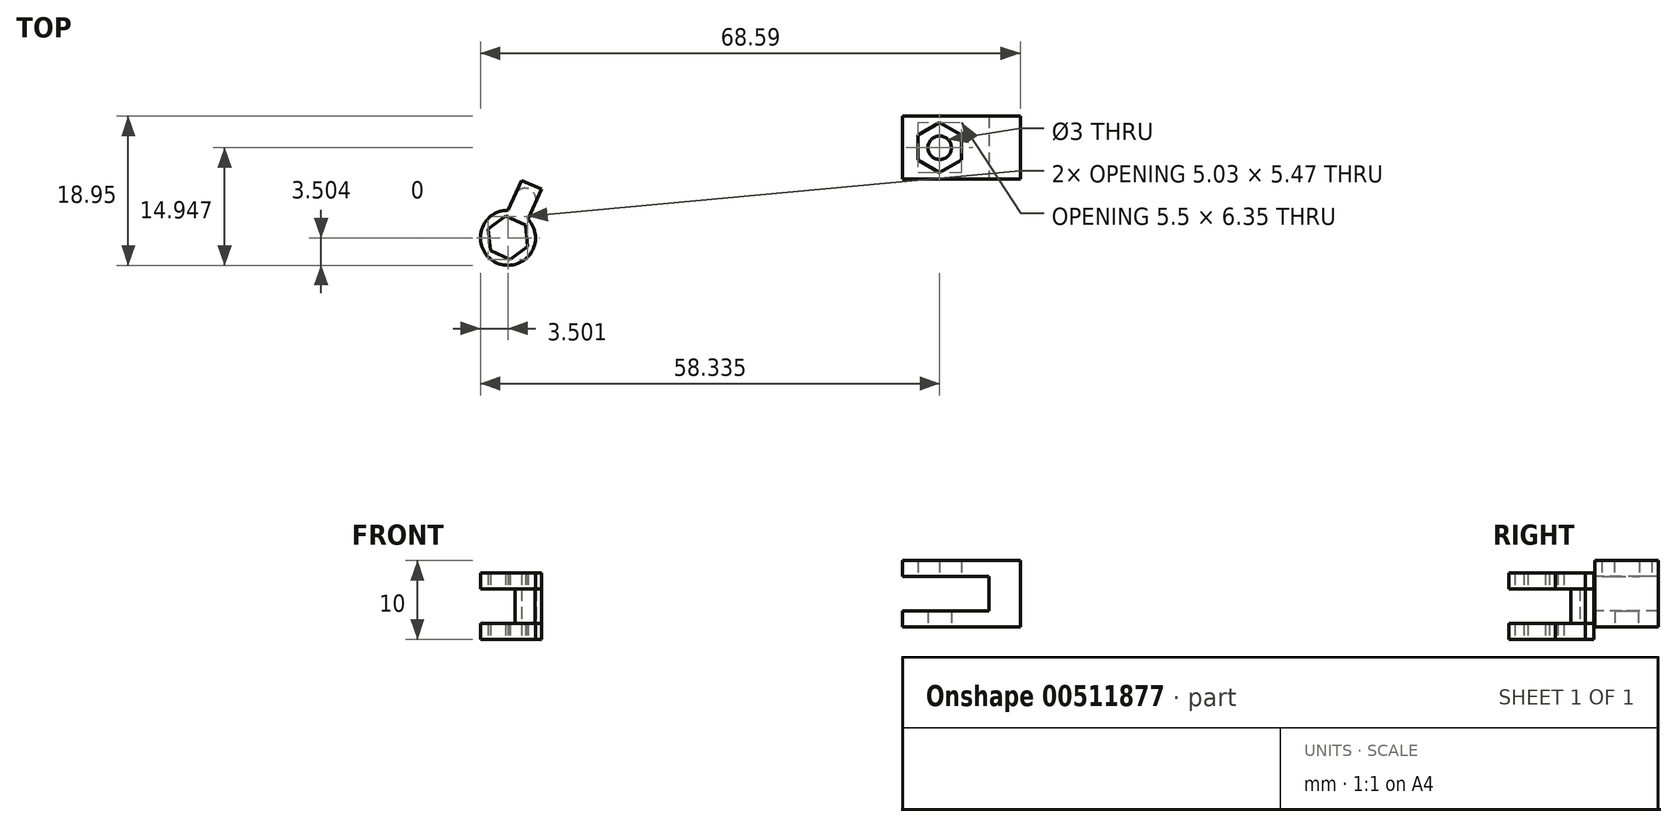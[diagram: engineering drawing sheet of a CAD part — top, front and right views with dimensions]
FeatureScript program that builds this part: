
annotation { "Feature Type Name" : "Feature", "Feature Type Description" : "" }
export const myFeature = defineFeature(function(context is Context, id is Id, definition is map)
    precondition{}
    {
        {
            var Q0;
            Q0=qCreatedBy(makeId("Top.planeOp"),FACE);
            var sketch = newSketch(context, id + "F0", { "sketchPlane" : qUnion([Q0])});
            skLineSegment(sketch, "E0.0", {"start": v(-17.86, 5.3) * mm, "end": v(-17.56, 2.57) * mm});
            skLineSegment(sketch, "E0.1", {"start": v(-17.56, 2.57) * mm, "end": v(-19.79, 0.95) * mm});
            skLineSegment(sketch, "E0.2", {"start": v(-19.79, 0.95) * mm, "end": v(-22.3, 2.06) * mm});
            skLineSegment(sketch, "E0.3", {"start": v(-22.3, 2.06) * mm, "end": v(-22.6, 4.8) * mm});
            skLineSegment(sketch, "E0.4", {"start": v(-22.6, 4.8) * mm, "end": v(-20.37, 6.42) * mm});
            skLineSegment(sketch, "E0.5", {"start": v(-20.37, 6.42) * mm, "end": v(-17.86, 5.3) * mm});
            skCircle(sketch, "E1", {"center": v(-20.08, 3.68) * mm, "radius": 3.5 * mm});
            skLineSegment(sketch, "E2", {"start": v(-20.37, 6.42) * mm, "end": v(-18.34, 10.99) * mm});
            skLineSegment(sketch, "E3", {"start": v(-17.86, 5.3) * mm, "end": v(-15.83, 9.88) * mm});
            skLineSegment(sketch, "E4", {"start": v(-15.83, 9.88) * mm, "end": v(-18.34, 10.99) * mm});
            skLineSegment(sketch, "E5", {"start": v(-20.37, 6.42) * mm, "end": v(-19.15, 9.16) * mm});
            skLineSegment(sketch, "E6", {"start": v(-16.64, 8.05) * mm, "end": v(-17.86, 5.3) * mm});
            skArc(sketch, "E7", {"start": v(-16.64, 8.05) * mm, "mid": v(-17.34, 9.86) * mm, "end": v(-19.15, 9.16) * mm});
            skSolve(sketch);
        }
        {
            var Q0;
            Q0 = qSketchRegion(id + "F0", true);
            var Q1;
            Q1 = qSketchRegion(id + "F2", true);
            extrude(context, id + "F1", {"entities" : qUnion([Q0, Q1]), "depth" : 8.4 * mm});
        }
        {
            var Q0;
            Q0=makeQuery(id+"F1.opExtrude","SWEPT_FACE",FACE,{"disambiguationData":[OSD([sQuery(id+"F0.wireOp",EDGE,"E3"),sQuery(id+"F0.wireOp",EDGE,"E6")])]});
            var sketch = newSketch(context, id + "F2", { "sketchPlane" : qUnion([Q0])});
            skLineSegment(sketch, "E8", {"start": v(2.61, 8.4) * mm, "end": v(2.61, 6.4) * mm});
            skLineSegment(sketch, "E9", {"start": v(2.61, 0) * mm, "end": v(2.61, 2) * mm});
            skLineSegment(sketch, "E10", {"start": v(2.61, 2) * mm, "end": v(-1.55, 2) * mm});
            skLineSegment(sketch, "E11", {"start": v(2.61, 6.4) * mm, "end": v(-1.55, 6.4) * mm});
            skLineSegment(sketch, "E12.bottom", {"start": v(2.61, 6.4) * mm, "end": v(-9.24, 6.4) * mm});
            skLineSegment(sketch, "E12.top", {"start": v(2.61, 2) * mm, "end": v(-9.24, 2) * mm});
            skLineSegment(sketch, "E12.left", {"start": v(2.61, 6.4) * mm, "end": v(2.61, 2) * mm});
            skLineSegment(sketch, "E12.right", {"start": v(-9.24, 6.4) * mm, "end": v(-9.24, 2) * mm});
            skSolve(sketch);
        }
        {
            var Q0;
            Q0 = qSketchRegion(id + "F2", true);
            extrude(context, id + "F3", {"entities" : qUnion([Q0]), "operationType" : NewBodyOperationType.REMOVE, "oppositeDirection" : true, "depth" : 25 * mm});
        }
        {
            var Q0;
            {var subQ0=sQuery(id+"F2.wireOp",EDGE,"E12.top");var subQ1=sQuery(id+"F2.wireOp",EDGE,"E12.bottom");Q0=makeQuery(id+"F3.boolean.opBoolean","COPY",FACE,{"disambiguationData":[TD([makeQuery(id+"F1.opExtrude","SWEPT_FACE",FACE,{"disambiguationData":[OSD([sQuery(id+"F0.wireOp",EDGE,"E0.1")])]})])],"derivedFrom":makeQuery(id+"F3.opExtrude","CAP_FACE",FACE,{"disambiguationData":[OSD([subQ1,subQ0,sQuery(id+"F2.wireOp",EDGE,"E12.left"),sQuery(id+"F2.wireOp",EDGE,"E12.right")])],"isStart":true})});}
            var sketch = newSketch(context, id + "F4", { "sketchPlane" : qUnion([Q0])});
            skPoint(sketch, "E13.oppositeSnap0", {"position": v(7.57, 2) * mm});
            skLineSegment(sketch, "E13.bottom", {"start": v(7.99, 6.4) * mm, "end": v(-1.42, 6.4) * mm});
            skLineSegment(sketch, "E13.top", {"start": v(7.99, 2) * mm, "end": v(-1.42, 2) * mm});
            skLineSegment(sketch, "E13.left", {"start": v(7.99, 6.4) * mm, "end": v(7.99, 2) * mm});
            skLineSegment(sketch, "E13.right", {"start": v(-1.42, 6.4) * mm, "end": v(-1.42, 2) * mm});
            skSolve(sketch);
        }
        {
            var Q0;
            Q0 = qSketchRegion(id + "F4", true);
            extrude(context, id + "F5", {"entities" : qUnion([Q0]), "operationType" : NewBodyOperationType.REMOVE, "oppositeDirection" : true, "depth" : 25 * mm});
        }
        {
            var Q0;
            Q0=makeQuery(id+"F5.boolean.opBoolean","MERGE",FACE,{"derivedFrom":[makeQuery(id+"F3.boolean.opBoolean","COPY",FACE,{"derivedFrom":makeQuery(id+"F3.opExtrude","SWEPT_FACE",FACE,{"disambiguationData":[OSD([sQuery(id+"F2.wireOp",EDGE,"E12.top")])]})}),makeQuery(id+"F5.opExtrude","SWEPT_FACE",FACE,{"disambiguationData":[OSD([sQuery(id+"F4.wireOp",EDGE,"E13.top")])]})]});
            var sketch = newSketch(context, id + "F6", { "sketchPlane" : qUnion([Q0])});
            skLineSegment(sketch, "E14", {"start": v(-20.37, 6.42) * mm, "end": v(-19.15, 9.16) * mm});
            skLineSegment(sketch, "E15", {"start": v(-17.86, 5.3) * mm, "end": v(-16.64, 8.05) * mm});
            skArc(sketch, "E16", {"start": v(-16.64, 8.05) * mm, "mid": v(-17.34, 9.86) * mm, "end": v(-19.15, 9.16) * mm});
            skSolve(sketch);
        }
        {
            var Q0;
            {var subQ0=sQuery(id+"F6.wireOp",EDGE,"E16");Q0=makeQuery(id+"F6.imprint","IMPRINT",FACE,{"disambiguationData":[TD([[makeQuery(id+"F6.imprint","IMPRINT",EDGE,{"derivedFrom":subQ0}),-1.0]])]});}
            extrude(context, id + "F7", {"entities" : qUnion([Q0]), "depth" : 4.4 * mm});
        }
        {
            var Q0;
            Q0=qCreatedBy(makeId("Top.planeOp"),FACE);
            var sketch = newSketch(context, id + "F8", { "sketchPlane" : qUnion([Q0])});
            skLineSegment(sketch, "E17.bottom", {"start": v(30, 19.13) * mm, "end": v(45, 19.13) * mm});
            skLineSegment(sketch, "E17.top", {"start": v(30, 11.13) * mm, "end": v(45, 11.13) * mm});
            skLineSegment(sketch, "E17.right", {"start": v(45, 19.13) * mm, "end": v(45, 11.13) * mm});
            skLineSegment(sketch, "E18", {"start": v(32, 16.71) * mm, "end": v(32, 13.54) * mm});
            skPoint(sketch, "E19", {"position": v(32, 15.13) * mm});
            skPoint(sketch, "E20", {"position": v(34.76, 15.13) * mm});
            skLineSegment(sketch, "E21.0", {"start": v(32, 16.71) * mm, "end": v(34.76, 18.3) * mm});
            skLineSegment(sketch, "E21.1", {"start": v(34.76, 18.3) * mm, "end": v(37.5, 16.71) * mm});
            skLineSegment(sketch, "E21.2", {"start": v(37.5, 16.71) * mm, "end": v(37.5, 13.54) * mm});
            skLineSegment(sketch, "E21.3", {"start": v(37.5, 13.54) * mm, "end": v(34.76, 11.95) * mm});
            skLineSegment(sketch, "E21.4", {"start": v(34.76, 11.95) * mm, "end": v(32, 13.54) * mm});
            skLineSegment(sketch, "E21.5", {"start": v(32, 13.54) * mm, "end": v(32, 16.71) * mm});
            skPoint(sketch, "E22.orphan", {"position": v(45, 15.13) * mm});
            skLineSegment(sketch, "E23", {"start": v(30, 11.13) * mm, "end": v(30, 19.13) * mm});
            skSolve(sketch);
        }
        {
            var Q0;
            Q0=makeQuery(id+"F8.imprint","IMPRINT",FACE,{"disambiguationData":[TD([[makeQuery(id+"F8.imprint","IMPRINT",EDGE,{"derivedFrom":sQuery(id+"F8.wireOp",EDGE,"E17.bottom")}),-1.0]])]});
            extrude(context, id + "F9", {"entities" : qUnion([Q0]), "depth" : 10 * mm});
        }
        {
            var Q0;
            Q0=makeQuery(id+"F9.opExtrude","SWEPT_FACE",FACE,{"disambiguationData":[OSD([sQuery(id+"F8.wireOp",EDGE,"E17.top")])]});
            var sketch = newSketch(context, id + "F10", { "sketchPlane" : qUnion([Q0])});
            skLineSegment(sketch, "E24", {"start": v(41, 10) * mm, "end": v(41, 0) * mm});
            skLineSegment(sketch, "E25", {"start": v(30, 8) * mm, "end": v(41, 8) * mm});
            skLineSegment(sketch, "E26", {"start": v(30, 3.6) * mm, "end": v(41, 3.6) * mm});
            skSolve(sketch);
        }
        {
            var Q0;
            {var subQ0=sQuery(id+"F10.wireOp",EDGE,"E25");Q0=makeQuery(id+"F10.imprint","IMPRINT",FACE,{"disambiguationData":[TD([[makeQuery(id+"F10.imprint","IMPRINT",EDGE,{"derivedFrom":subQ0}),-1.0]])]});}
            extrude(context, id + "F11", {"entities" : qUnion([Q0]), "operationType" : NewBodyOperationType.REMOVE, "oppositeDirection" : true, "depth" : 25 * mm});
        }
        {
            var Q0;
            Q0=makeQuery(id+"F9.opExtrude","SWEPT_FACE",FACE,{"disambiguationData":[OSD([sQuery(id+"F8.wireOp",EDGE,"E17.bottom")])]});
            var sketch = newSketch(context, id + "F12", { "sketchPlane" : qUnion([Q0])});
            skPoint(sketch, "E27", {"position": v(-30, 1.6) * mm});
            skLineSegment(sketch, "E28", {"start": v(-30, 1.6) * mm, "end": v(-45, 1.6) * mm});
            skLineSegment(sketch, "E29", {"start": v(-45, 1.6) * mm, "end": v(-45, 3.6) * mm});
            skLineSegment(sketch, "E30", {"start": v(-45, 3.6) * mm, "end": v(-30, 3.6) * mm});
            skSolve(sketch);
        }
        {
            var Q0;
            {var subQ0=sQuery(id+"F12.wireOp",EDGE,"E28");Q0=makeQuery(id+"F12.imprint","IMPRINT",FACE,{"disambiguationData":[TD([[makeQuery(id+"F12.imprint","IMPRINT",EDGE,{"derivedFrom":subQ0}),1.0]])]});}
            extrude(context, id + "F13", {"entities" : qUnion([Q0]), "operationType" : NewBodyOperationType.REMOVE, "oppositeDirection" : true, "depth" : 25 * mm});
        }
        {
            var Q0;
            {var subQ1=sQuery(id+"F8.wireOp",EDGE,"E23");Q0=makeQuery(id+"F11.boolean.opBoolean","SPLIT",FACE,{"disambiguationData":[TD([makeQuery(id+"F11.opExtrude","SWEPT_FACE",FACE,{"disambiguationData":[OSD([sQuery(id+"F10.wireOp",EDGE,"E26")])]})])],"derivedFrom":makeQuery(id+"F9.opExtrude","SWEPT_FACE",FACE,{"disambiguationData":[OSD([subQ1])]})});}
            extrude(context, id + "F14", {"entities" : qUnion([Q0]), "operationType" : NewBodyOperationType.ADD, "oppositeDirection" : true, "depth" : 10 * mm});
        }
        {
            var Q0;
            {var subQ0=sQuery(id+"F12.wireOp",EDGE,"E28");Q0=makeQuery(id+"F14.boolean.opBoolean","MERGE",FACE,{"derivedFrom":[makeQuery(id+"F13.boolean.opBoolean","COPY",FACE,{"derivedFrom":makeQuery(id+"F13.opExtrude","SWEPT_FACE",FACE,{"disambiguationData":[OSD([subQ0])]})}),makeQuery(id+"F14.opExtrude","SWEPT_FACE",FACE,{"disambiguationData":[OSD([sQuery(id+"F8.wireOp",EDGE,"E17.bottom"),sQuery(id+"F8.wireOp",EDGE,"E23"),subQ0])]})]});}
            var sketch = newSketch(context, id + "F15", { "sketchPlane" : qUnion([Q0])});
            skPoint(sketch, "E31.orphan", {"position": v(34.76, -11.13) * mm});
            skCircle(sketch, "E32", {"center": v(34.76, -15.13) * mm, "radius": 1.5 * mm});
            skSolve(sketch);
        }
        {
            var Q0;
            Q0=makeQuery(id+"F15.imprint","IMPRINT",FACE,{"disambiguationData":[TD([[makeQuery(id+"F15.imprint","IMPRINT",EDGE,{"derivedFrom":sQuery(id+"F15.wireOp",EDGE,"E32")}),1.0]])]});
            extrude(context, id + "F16", {"entities" : qUnion([Q0]), "operationType" : NewBodyOperationType.REMOVE, "oppositeDirection" : true, "depth" : 25 * mm});
        }
    });
